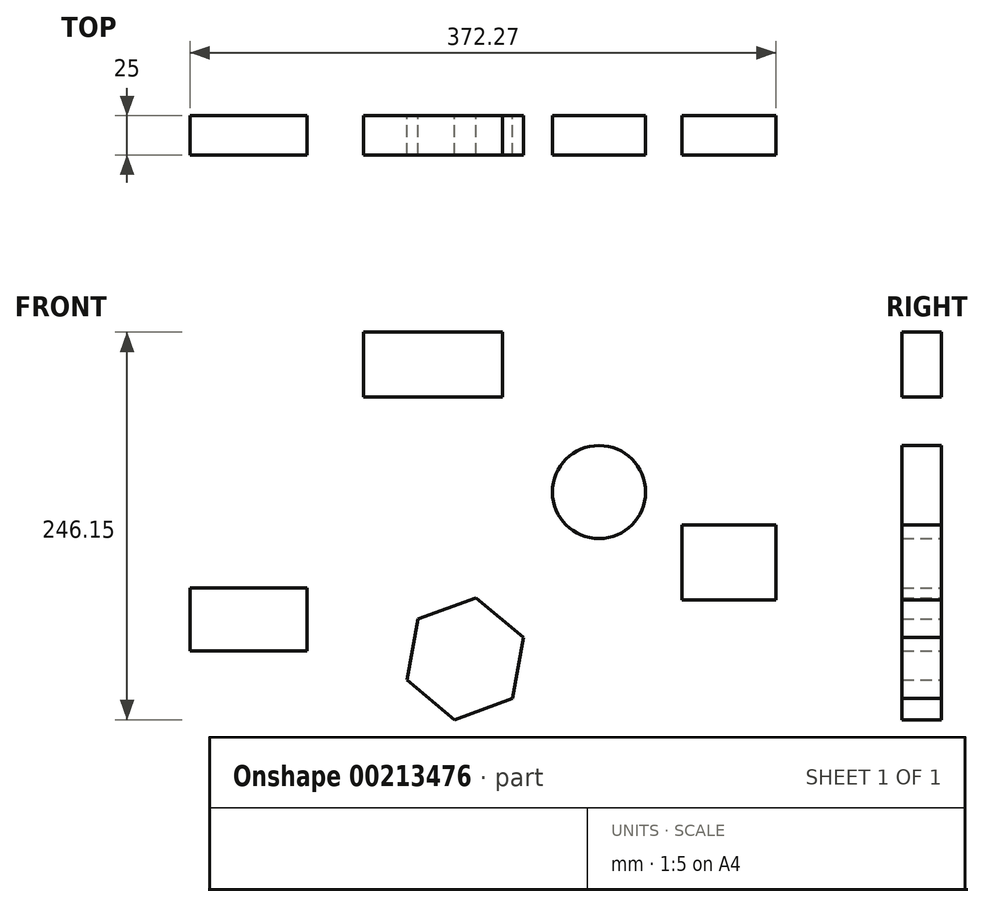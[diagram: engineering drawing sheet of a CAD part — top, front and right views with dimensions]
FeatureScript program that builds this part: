
annotation { "Feature Type Name" : "Feature", "Feature Type Description" : "" }
export const myFeature = defineFeature(function(context is Context, id is Id, definition is map)
    precondition{}
    {
        {
            var Q0;
            Q0=qCreatedBy(makeId("Front.planeOp"),FACE);
            var sketch = newSketch(context, id + "F0", { "sketchPlane" : qUnion([Q0])});
            skLineSegment(sketch, "E0.bottom", {"start": v(-137.77, 61.12) * mm, "end": v(-77.98, 61.12) * mm});
            skLineSegment(sketch, "E0.top", {"start": v(-137.77, 13.4) * mm, "end": v(-77.98, 13.4) * mm});
            skLineSegment(sketch, "E0.left", {"start": v(-137.77, 61.12) * mm, "end": v(-137.77, 13.4) * mm});
            skLineSegment(sketch, "E0.right", {"start": v(-77.98, 61.12) * mm, "end": v(-77.98, 13.4) * mm});
            skLineSegment(sketch, "E1.bottom", {"start": v(-450.25, 21.12) * mm, "end": v(-375.79, 21.12) * mm});
            skLineSegment(sketch, "E1.top", {"start": v(-450.25, -19.17) * mm, "end": v(-375.79, -19.17) * mm});
            skLineSegment(sketch, "E1.left", {"start": v(-450.25, 21.12) * mm, "end": v(-450.25, -19.17) * mm});
            skLineSegment(sketch, "E1.right", {"start": v(-375.79, 21.12) * mm, "end": v(-375.79, -19.17) * mm});
            skLineSegment(sketch, "E2.bottom", {"start": v(-339.88, 183.41) * mm, "end": v(-251.7, 183.41) * mm});
            skLineSegment(sketch, "E2.top", {"start": v(-339.88, 142.33) * mm, "end": v(-251.7, 142.33) * mm});
            skLineSegment(sketch, "E2.left", {"start": v(-339.88, 183.41) * mm, "end": v(-339.88, 142.33) * mm});
            skLineSegment(sketch, "E2.right", {"start": v(-251.7, 183.41) * mm, "end": v(-251.7, 142.33) * mm});
            skCircle(sketch, "E3", {"center": v(-190.44, 81.86) * mm, "radius": 29.57 * mm});
            skCircle(sketch, "E4.cCircle", {"center": v(-275.45, -24) * mm, "radius": 34.07 * mm, "construction": true});
            skLineSegment(sketch, "E4.0", {"start": v(-305.56, 1.32) * mm, "end": v(-268.58, 14.73) * mm});
            skLineSegment(sketch, "E4.1", {"start": v(-268.58, 14.73) * mm, "end": v(-238.47, -10.59) * mm});
            skLineSegment(sketch, "E4.2", {"start": v(-238.47, -10.59) * mm, "end": v(-245.35, -49.32) * mm});
            skLineSegment(sketch, "E4.3", {"start": v(-245.35, -49.32) * mm, "end": v(-282.33, -62.74) * mm});
            skLineSegment(sketch, "E4.4", {"start": v(-282.33, -62.74) * mm, "end": v(-312.44, -37.42) * mm});
            skLineSegment(sketch, "E4.5", {"start": v(-312.44, -37.42) * mm, "end": v(-305.56, 1.32) * mm});
            skPoint(sketch, "E4.0.midPoint", {"position": v(-287.07, 8.02) * mm});
            skSolve(sketch);
        }
        {
            var Q0;
            Q0 = qSketchRegion(id + "F0", true);
            extrude(context, id + "F1", {"entities" : qUnion([Q0]), "depth" : 25 * mm});
        }
    });
